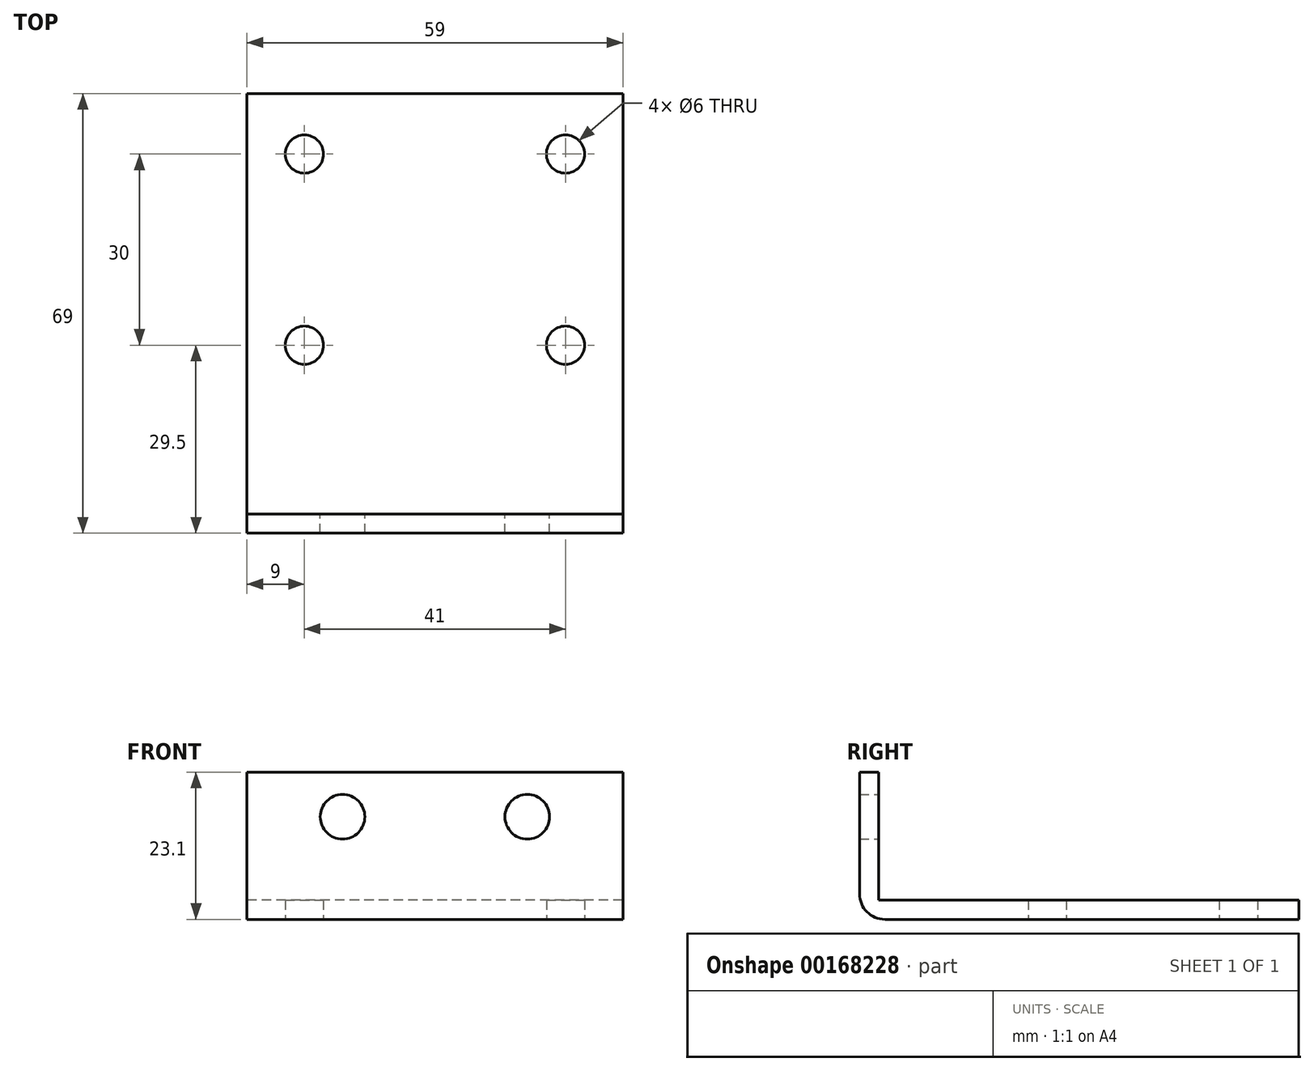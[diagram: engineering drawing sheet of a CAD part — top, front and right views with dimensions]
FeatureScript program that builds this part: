
annotation { "Feature Type Name" : "Feature", "Feature Type Description" : "" }
export const myFeature = defineFeature(function(context is Context, id is Id, definition is map)
    precondition{}
    {
        {
            var Q0;
            Q0=qCreatedBy(makeId("Front.planeOp"),FACE);
            var sketch = newSketch(context, id + "F0", { "sketchPlane" : qUnion([Q0])});
            skLineSegment(sketch, "E0.bottom", {"start": v(29.5, 11.55) * mm, "end": v(-29.5, 11.55) * mm});
            skLineSegment(sketch, "E0.top", {"start": v(29.5, -11.55) * mm, "end": v(-29.5, -11.55) * mm});
            skLineSegment(sketch, "E0.left", {"start": v(29.5, 11.55) * mm, "end": v(29.5, -11.55) * mm});
            skLineSegment(sketch, "E0.right", {"start": v(-29.5, 11.55) * mm, "end": v(-29.5, -11.55) * mm});
            skPoint(sketch, "E0.middle", {"position": v(0, 0) * mm});
            skCircle(sketch, "E1", {"center": v(-14.5, 4.55) * mm, "radius": 3.5 * mm});
            skCircle(sketch, "E2", {"center": v(14.5, 4.55) * mm, "radius": 3.5 * mm});
            skSolve(sketch);
        }
        {
            var Q0;
            Q0 = qSketchRegion(id + "F0", true);
            extrude(context, id + "F1", {"entities" : qUnion([Q0]), "endBound" : BoundingType.SYMMETRIC, "depth" : 3 * mm});
        }
        {
            var Q0;
            Q0=makeQuery(id+"F1.opExtrude","SWEPT_FACE",FACE,{"disambiguationData":[OSD([sQuery(id+"F0.wireOp",EDGE,"E0.top")])]});
            cPlane(context, id + "F2", {"entities" : qUnion([Q0]), "cplaneType" : CPlaneType.OFFSET, "offset" : 0 * mm, "width" : 150 * mm, "height" : 150 * mm});
        }
        {
            var Q0;
            Q0=qCreatedBy(id+"F2.planeOp",FACE);
            var sketch = newSketch(context, id + "F3", { "sketchPlane" : qUnion([Q0])});
            skLineSegment(sketch, "E3.0", {"start": v(29.5, -1.5) * mm, "end": v(-29.5, -1.5) * mm});
            skLineSegment(sketch, "E4.bottom", {"start": v(-29.5, -1.5) * mm, "end": v(29.5, -1.5) * mm});
            skLineSegment(sketch, "E4.top", {"start": v(-29.5, -67.5) * mm, "end": v(29.5, -67.5) * mm});
            skLineSegment(sketch, "E4.left", {"start": v(-29.5, -1.5) * mm, "end": v(-29.5, -67.5) * mm});
            skLineSegment(sketch, "E4.right", {"start": v(29.5, -1.5) * mm, "end": v(29.5, -67.5) * mm});
            skCircle(sketch, "E5", {"center": v(20.5, -58) * mm, "radius": 3 * mm});
            skCircle(sketch, "E6", {"center": v(20.5, -28) * mm, "radius": 3 * mm});
            skLineSegment(sketch, "E7", {"start": v(0, 6.33) * mm, "end": v(0, -79.01) * mm, "construction": true});
            skPoint(sketch, "E7.startSnap0", {"position": v(0, -1.5) * mm});
            skPoint(sketch, "E7.endSnap0", {"position": v(0, -67.5) * mm});
            skCircle(sketch, "E8.MirrorC", {"center": v(-20.5, -28) * mm, "radius": 3 * mm});
            skCircle(sketch, "E9.MirrorC", {"center": v(-20.5, -58) * mm, "radius": 3 * mm});
            skSolve(sketch);
        }
        {
            var Q0;
            Q0 = qSketchRegion(id + "F3", true);
            extrude(context, id + "F4", {"entities" : qUnion([Q0]), "operationType" : NewBodyOperationType.ADD, "oppositeDirection" : true, "depth" : 3 * mm});
        }
        {
            var Q0;
            Q0=makeQuery(id+"F1.opExtrude","CAP_EDGE",EDGE,{"disambiguationData":[OSD([sQuery(id+"F0.wireOp",EDGE,"E0.top")])],"isStart":false});
            fillet(context, id + "F5", {"entities" : qUnion([Q0]), "radius" : 4 * mm, "tangentPropagation" : true, "allowEdgeOverflow" : false});
        }
    });
